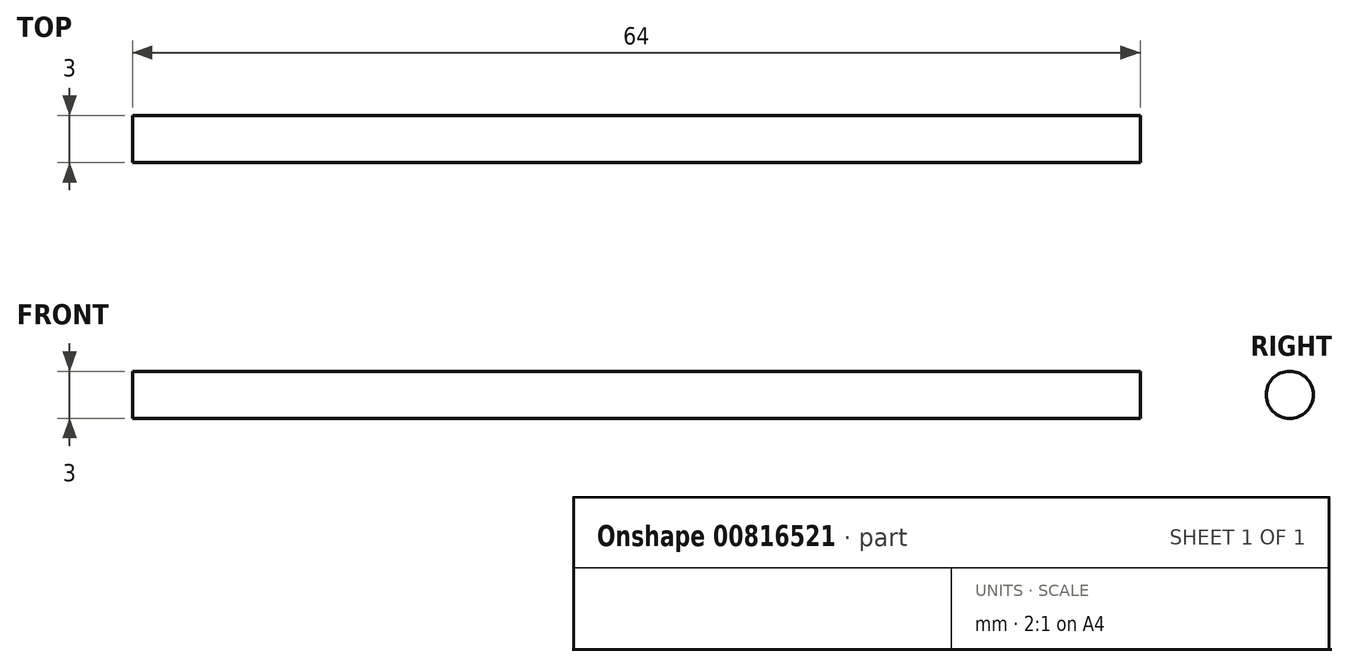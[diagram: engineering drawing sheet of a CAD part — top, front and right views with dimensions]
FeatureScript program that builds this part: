
annotation { "Feature Type Name" : "Feature", "Feature Type Description" : "" }
export const myFeature = defineFeature(function(context is Context, id is Id, definition is map)
    precondition{}
    {
        {
            var Q0;
            Q0=qCreatedBy(makeId("Right.planeOp"),FACE);
            var sketch = newSketch(context, id + "F0", { "sketchPlane" : qUnion([Q0])});
            skCircle(sketch, "E0", {"center": v(0, 0) * mm, "radius": 1.5 * mm});
            skSolve(sketch);
        }
        {
            var Q0;
            Q0 = qSketchRegion(id + "F0", true);
            extrude(context, id + "F1", {"entities" : qUnion([Q0]), "depth" : 64 * mm, "offsetDistance" : 25 * mm});
        }
    });
